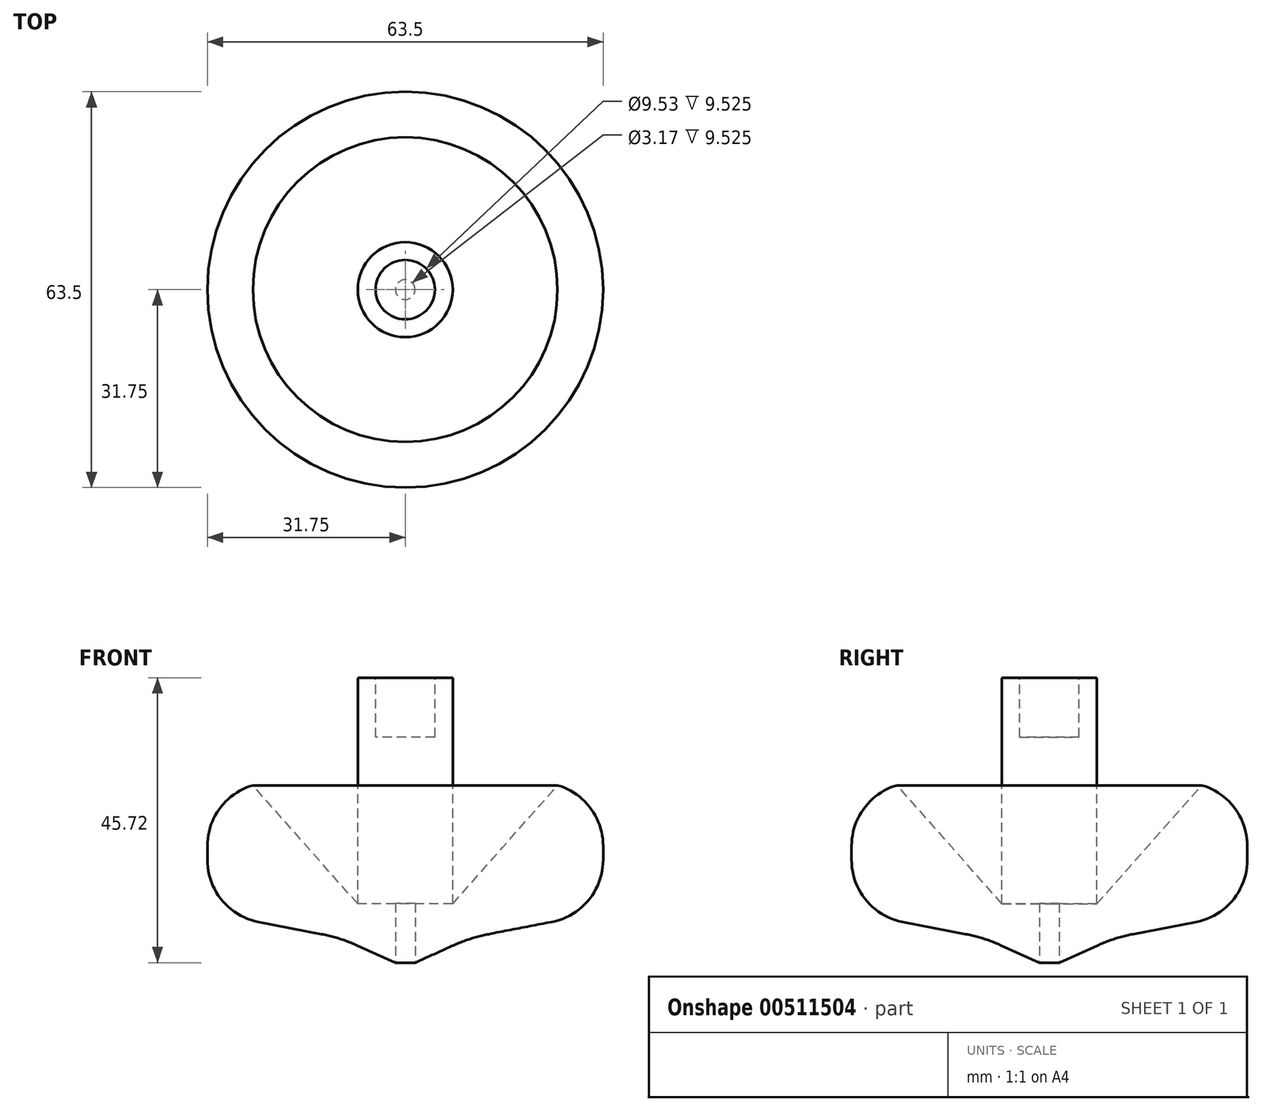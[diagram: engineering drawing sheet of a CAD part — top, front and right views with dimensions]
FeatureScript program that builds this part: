
annotation { "Feature Type Name" : "Feature", "Feature Type Description" : "" }
export const myFeature = defineFeature(function(context is Context, id is Id, definition is map)
    precondition{}
    {
        {
            var Q0;
            Q0=qCreatedBy(makeId("Front.planeOp"),FACE);
            var sketch = newSketch(context, id + "F0", { "sketchPlane" : qUnion([Q0])});
            skLineSegment(sketch, "E0", {"start": v(31.75, 8.13) * mm, "end": v(31.75, 28.45) * mm});
            skLineSegment(sketch, "E1", {"start": v(31.75, 28.45) * mm, "end": v(24.44, 28.45) * mm});
            skLineSegment(sketch, "E2", {"start": v(24.44, 28.45) * mm, "end": v(7.62, 9.44) * mm});
            skLineSegment(sketch, "E3", {"start": v(7.62, 9.44) * mm, "end": v(7.62, 45.72) * mm});
            skLineSegment(sketch, "E4", {"start": v(7.62, 45.72) * mm, "end": v(0, 45.72) * mm});
            skLineSegment(sketch, "E5", {"start": v(0, 45.72) * mm, "end": v(0, 0) * mm});
            skLineSegment(sketch, "E6", {"start": v(10.5, 4.02) * mm, "end": v(31.75, 8.13) * mm});
            skLineSegment(sketch, "E7", {"start": v(0, 0) * mm, "end": v(1.59, 0) * mm});
            skLineSegment(sketch, "E8", {"start": v(1.59, 0) * mm, "end": v(10.5, 4.02) * mm});
            skSolve(sketch);
        }
        {
            var Q0;
            Q0=qSketchRegion(id+"F0",true);
            var Q1;
            Q1=sQuery(id+"F0.wireOp",EDGE,"E5");
            revolve(context, id + "F1", {"entities" : qUnion([Q0]), "axis" : qUnion([Q1]), "revolveType" : RevolveType.FULL});
        }
        {
            var Q0;
            Q0=makeQuery(id+"F1.opRevolve","SWEPT_FACE",FACE,{"disambiguationData":[OSD([sQuery(id+"F0.wireOp",EDGE,"E0")])]});
            fillet(context, id + "F2", {"entities" : qUnion([Q0]), "radius" : 10.16 * mm, "tangentPropagation" : true, "allowEdgeOverflow" : false});
        }
        {
            var Q0;
            Q0=makeQuery(id+"F1.opRevolve","SWEPT_EDGE",EDGE,{"disambiguationData":[OSD([sQuery(id+"F0.wireOp",EDGE,"E6"),sQuery(id+"F0.wireOp",EDGE,"E8")])]});
            fillet(context, id + "F3", {"entities" : qUnion([Q0]), "radius" : 25.4 * mm, "tangentPropagation" : true, "allowEdgeOverflow" : false});
        }
        {
            var Q0;
            Q0=makeQuery(id+"F1.opRevolve","SWEPT_FACE",FACE,{"disambiguationData":[OSD([sQuery(id+"F0.wireOp",EDGE,"E4")])]});
            var sketch = newSketch(context, id + "F4", { "sketchPlane" : qUnion([Q0])});
            skCircle(sketch, "E9", {"center": v(0, 0) * mm, "radius": 4.76 * mm});
            skSolve(sketch);
        }
        {
            var Q0;
            Q0=qSketchRegion(id+"F4",true);
            extrude(context, id + "F5", {"entities" : qUnion([Q0]), "operationType" : NewBodyOperationType.REMOVE, "oppositeDirection" : true, "depth" : 9.52 * mm});
        }
        {
            var Q0;
            Q0=qCreatedBy(makeId("Top.planeOp"),FACE);
            var sketch = newSketch(context, id + "F6", { "sketchPlane" : qUnion([Q0])});
            skCircle(sketch, "E10", {"center": v(0, 0) * mm, "radius": 1.59 * mm});
            skSolve(sketch);
        }
        {
            var Q0;
            Q0=qSketchRegion(id+"F6",true);
            extrude(context, id + "F7", {"entities" : qUnion([Q0]), "operationType" : NewBodyOperationType.REMOVE, "depth" : 9.52 * mm});
        }
    });
